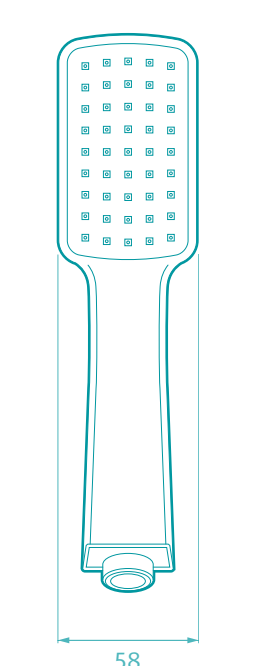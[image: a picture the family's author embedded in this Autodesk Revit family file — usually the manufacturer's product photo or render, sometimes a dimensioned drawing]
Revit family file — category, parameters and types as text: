
# Revit family: 434470001_Teleducha_Nogal
name_source: partatom
category: Plumbing Fixtures
units: mm (PartAtom-declared; Revit-internal decimal feet)

## family parameters
Always vertical = Yes
Cut with Voids When Loaded = No
OmniClass Number = 23.31.11.00
OmniClass Title = Faucets
Part Type = Normal
Room Calculation Point = No
Round Connector Dimension = Use Diameter
Shared = No
Work Plane-Based = No

## types (1)
- 434470001_Teleducha_Nogal
    Alto = 231 mm  [stored 0.757874 ft]
    Ancho = 58 mm  [stored 0.190289 ft]
    Capacidad de flujo = A 80 psi: 9.3 l/min.
    Creado por = BIMBAU
    Default Elevation = 0 mm  [stored 0 ft]
    Description = La teleducha Nogal con tamaño medio y chorro tipo agua focalizado ofrece mayor practicidad, ideal para consumidores que buscan cobertura direccionada.
    Dimensiones generales del producto = 90 x 240 x 143 mm
    Diámetro abasto = 13 mm
    Fecha de creación = 14/04/2021
    Garantía = 30 años Grival - 2 años Acabados.
    Manufacturer = Corona.
    Material = Corona_Cromado
    Material 2 = Corona_Plastico_Gris
    Model = 434470001_Teleducha_Nogal
    Peso neto = 340 g. - 0.7 lb.
    Presión máxima recomendada = 125 psi.
    Presión mínima recomendada = 20 psi.
    Profundidad = 68 mm
    Recubrimientos = Resistente a la corrosión, pelado y decoloración por agua. Recubrimientos no tóxicos. Producto para uso doméstico.
    Referencia = 434470001
    Temperatura de uso = 5° C a 71° C.

note: [stored X ft] marks values corroborated as IEEE doubles in the binary element streams (Revit-internal decimal feet)

## geometry (parser evidence)
native form markers: Sweep x3
no freeform markers — native parametric forms only
